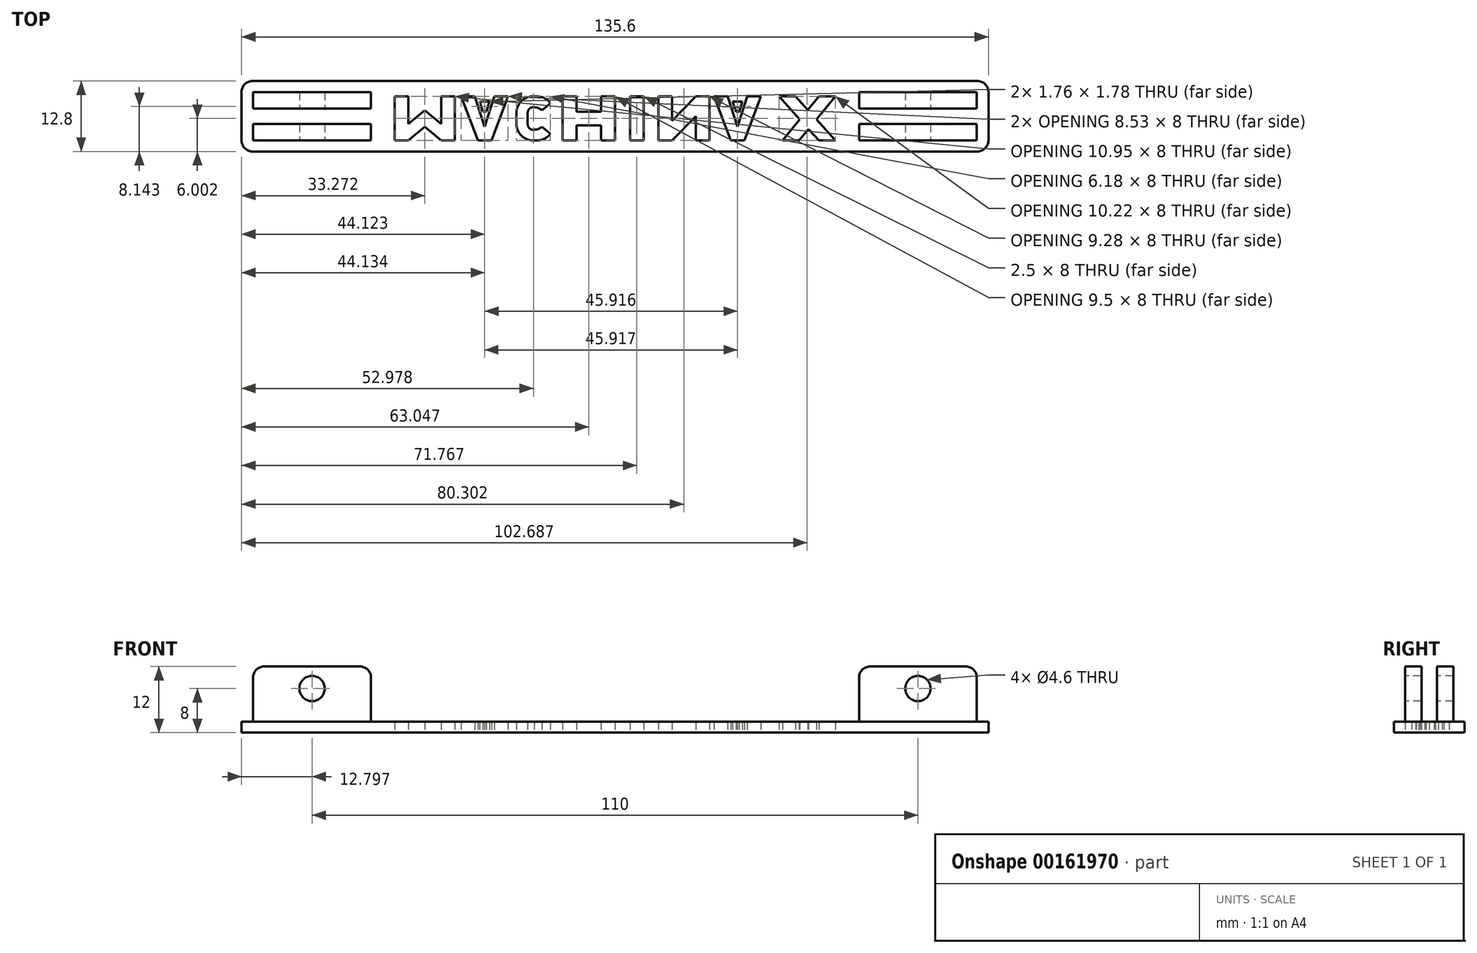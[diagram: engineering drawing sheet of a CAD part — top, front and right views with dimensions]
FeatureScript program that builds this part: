
annotation { "Feature Type Name" : "Feature", "Feature Type Description" : "" }
export const myFeature = defineFeature(function(context is Context, id is Id, definition is map)
    precondition{}
    {
        {
            var Q0;
            Q0=qCreatedBy(makeId("Top.planeOp"),FACE);
            var sketch = newSketch(context, id + "F0", { "sketchPlane" : qUnion([Q0])});
            skLineSegment(sketch, "E0.bottom", {"start": v(-66.14, 19.98) * mm, "end": v(65.46, 19.98) * mm});
            skLineSegment(sketch, "E0.top", {"start": v(-66.14, 7.18) * mm, "end": v(65.46, 7.18) * mm});
            skLineSegment(sketch, "E0.left", {"start": v(-68.14, 17.98) * mm, "end": v(-68.14, 9.18) * mm});
            skLineSegment(sketch, "E0.right", {"start": v(67.46, 17.98) * mm, "end": v(67.46, 9.18) * mm});
            skPoint(sketch, "E1.visualSharp", {"position": v(-68.14, 19.98) * mm});
            skArc(sketch, "E1.filletArc", {"start": v(-66.14, 19.98) * mm, "mid": v(-67.56, 19.4) * mm, "end": v(-68.14, 17.98) * mm});
            skPoint(sketch, "E2.visualSharp", {"position": v(-68.14, 7.18) * mm});
            skArc(sketch, "E2.filletArc", {"start": v(-68.14, 9.18) * mm, "mid": v(-67.56, 7.77) * mm, "end": v(-66.14, 7.18) * mm});
            skPoint(sketch, "E3.visualSharp", {"position": v(67.46, 19.98) * mm});
            skArc(sketch, "E3.filletArc", {"start": v(67.46, 17.98) * mm, "mid": v(66.87, 19.4) * mm, "end": v(65.46, 19.98) * mm});
            skPoint(sketch, "E4.visualSharp", {"position": v(67.46, 7.18) * mm});
            skArc(sketch, "E4.filletArc", {"start": v(65.46, 7.18) * mm, "mid": v(66.87, 7.77) * mm, "end": v(67.46, 9.18) * mm});
            skSolve(sketch);
        }
        {
            var Q0;
            Q0 = qSketchRegion(id + "F0", true);
            extrude(context, id + "F1", {"entities" : qUnion([Q0]), "depth" : 2 * mm});
        }
        {
            var Q0;
            Q0=makeQuery(id+"F1.opExtrude","CAP_FACE",FACE,{"disambiguationData":[OSD([sQuery(id+"F0.wireOp",EDGE,"E0.bottom"),sQuery(id+"F0.wireOp",EDGE,"E0.top"),sQuery(id+"F0.wireOp",EDGE,"E0.left"),sQuery(id+"F0.wireOp",EDGE,"E0.right"),sQuery(id+"F0.wireOp",EDGE,"E1.filletArc"),sQuery(id+"F0.wireOp",EDGE,"E2.filletArc"),sQuery(id+"F0.wireOp",EDGE,"E3.filletArc"),sQuery(id+"F0.wireOp",EDGE,"E4.filletArc")])],"isStart":false});
            var sketch = newSketch(context, id + "F2", { "sketchPlane" : qUnion([Q0])});
            skLineSegment(sketch, "E5.0", {"start": v(-68.14, 17.98) * mm, "end": v(-68.14, 9.18) * mm, "construction": true});
            skLineSegment(sketch, "E6.0", {"start": v(-66.14, 7.18) * mm, "end": v(65.46, 7.18) * mm, "construction": true});
            skLineSegment(sketch, "E7", {"start": v(-68.14, 13.58) * mm, "end": v(-66.04, 13.58) * mm, "construction": true});
            skPoint(sketch, "E7.endSnap0", {"position": v(-68.14, 13.58) * mm});
            skLineSegment(sketch, "E8", {"start": v(-66.04, 13.58) * mm, "end": v(-44.64, 13.58) * mm, "construction": true});
            skLineSegment(sketch, "E9", {"start": v(-44.64, 13.58) * mm, "end": v(43.96, 13.58) * mm, "construction": true});
            skLineSegment(sketch, "E10", {"start": v(43.96, 13.58) * mm, "end": v(65.36, 13.58) * mm, "construction": true});
            skLineSegment(sketch, "E11", {"start": v(65.36, 13.58) * mm, "end": v(67.46, 13.58) * mm, "construction": true});
            skLineSegment(sketch, "E12", {"start": v(-0.34, 7.18) * mm, "end": v(-0.34, 9.18) * mm, "construction": true});
            skLineSegment(sketch, "E13", {"start": v(-0.34, 9.18) * mm, "end": v(-0.34, 12.18) * mm, "construction": true});
            skLineSegment(sketch, "E14", {"start": v(-0.34, 12.18) * mm, "end": v(-0.34, 14.98) * mm, "construction": true});
            skPoint(sketch, "E14.endSnap0", {"position": v(-0.34, 10.68) * mm});
            skLineSegment(sketch, "E15", {"start": v(-0.34, 14.98) * mm, "end": v(-0.34, 17.98) * mm, "construction": true});
            skLineSegment(sketch, "E16", {"start": v(-0.34, 17.98) * mm, "end": v(-0.34, 19.98) * mm, "construction": true});
            skLineSegment(sketch, "E17.bottom", {"start": v(-66.04, 9.18) * mm, "end": v(-44.64, 9.18) * mm});
            skLineSegment(sketch, "E17.top", {"start": v(-66.04, 12.18) * mm, "end": v(-44.64, 12.18) * mm});
            skLineSegment(sketch, "E17.left", {"start": v(-66.04, 9.18) * mm, "end": v(-66.04, 12.18) * mm});
            skLineSegment(sketch, "E17.right", {"start": v(-44.64, 9.18) * mm, "end": v(-44.64, 12.18) * mm});
            skLineSegment(sketch, "E18.bottom", {"start": v(-66.04, 17.98) * mm, "end": v(-44.64, 17.98) * mm});
            skLineSegment(sketch, "E18.top", {"start": v(-66.04, 14.98) * mm, "end": v(-44.64, 14.98) * mm});
            skLineSegment(sketch, "E18.left", {"start": v(-66.04, 17.98) * mm, "end": v(-66.04, 14.98) * mm});
            skLineSegment(sketch, "E18.right", {"start": v(-44.64, 17.98) * mm, "end": v(-44.64, 14.98) * mm});
            skLineSegment(sketch, "E19.bottom", {"start": v(65.36, 17.98) * mm, "end": v(43.96, 17.98) * mm});
            skLineSegment(sketch, "E19.top", {"start": v(65.36, 14.98) * mm, "end": v(43.96, 14.98) * mm});
            skLineSegment(sketch, "E19.left", {"start": v(65.36, 17.98) * mm, "end": v(65.36, 14.98) * mm});
            skLineSegment(sketch, "E19.right", {"start": v(43.96, 17.98) * mm, "end": v(43.96, 14.98) * mm});
            skLineSegment(sketch, "E20.bottom", {"start": v(65.36, 9.18) * mm, "end": v(43.96, 9.18) * mm});
            skLineSegment(sketch, "E20.top", {"start": v(65.36, 12.18) * mm, "end": v(43.96, 12.18) * mm});
            skLineSegment(sketch, "E20.left", {"start": v(65.36, 9.18) * mm, "end": v(65.36, 12.18) * mm});
            skLineSegment(sketch, "E20.right", {"start": v(43.96, 9.18) * mm, "end": v(43.96, 12.18) * mm});
            skSolve(sketch);
        }
        {
            var Q0;
            Q0 = qSketchRegion(id + "F2", true);
            extrude(context, id + "F3", {"entities" : qUnion([Q0]), "operationType" : NewBodyOperationType.ADD, "depth" : 10 * mm});
        }
        {
            var Q0;
            Q0=makeQuery(id+"F3.opExtrude","CAP_EDGE",EDGE,{"disambiguationData":[OSD([sQuery(id+"F2.wireOp",EDGE,"E18.left")])],"isStart":false});
            var Q1;
            Q1=makeQuery(id+"F3.opExtrude","CAP_EDGE",EDGE,{"disambiguationData":[OSD([sQuery(id+"F2.wireOp",EDGE,"E17.left")])],"isStart":false});
            var Q2;
            Q2=makeQuery(id+"F3.opExtrude","CAP_EDGE",EDGE,{"disambiguationData":[OSD([sQuery(id+"F2.wireOp",EDGE,"E18.right")])],"isStart":false});
            var Q3;
            Q3=makeQuery(id+"F3.opExtrude","CAP_EDGE",EDGE,{"disambiguationData":[OSD([sQuery(id+"F2.wireOp",EDGE,"E17.right")])],"isStart":false});
            var Q4;
            Q4=makeQuery(id+"F3.opExtrude","CAP_EDGE",EDGE,{"disambiguationData":[OSD([sQuery(id+"F2.wireOp",EDGE,"E19.right")])],"isStart":false});
            var Q5;
            Q5=makeQuery(id+"F3.opExtrude","CAP_EDGE",EDGE,{"disambiguationData":[OSD([sQuery(id+"F2.wireOp",EDGE,"E19.left")])],"isStart":false});
            var Q6;
            Q6=makeQuery(id+"F3.opExtrude","CAP_EDGE",EDGE,{"disambiguationData":[OSD([sQuery(id+"F2.wireOp",EDGE,"E20.left")])],"isStart":false});
            var Q7;
            Q7=makeQuery(id+"F3.opExtrude","CAP_EDGE",EDGE,{"disambiguationData":[OSD([sQuery(id+"F2.wireOp",EDGE,"E20.right")])],"isStart":false});
            fillet(context, id + "F4", {"entities" : qUnion([Q0, Q1, Q2, Q3, Q4, Q5, Q6, Q7]), "radius" : 2 * mm, "tangentPropagation" : true, "allowEdgeOverflow" : false});
        }
        {
            var Q0;
            Q0=makeQuery(id+"F3.opExtrude","SWEPT_FACE",FACE,{"disambiguationData":[OSD([sQuery(id+"F2.wireOp",EDGE,"E17.bottom")])]});
            var sketch = newSketch(context, id + "F5", { "sketchPlane" : qUnion([Q0])});
            skLineSegment(sketch, "E21.0", {"start": v(-66.04, 2) * mm, "end": v(-44.64, 2) * mm, "construction": true});
            skLineSegment(sketch, "E22.0", {"start": v(65.36, 2) * mm, "end": v(43.96, 2) * mm, "construction": true});
            skLineSegment(sketch, "E23", {"start": v(-55.34, 2) * mm, "end": v(-55.34, 8) * mm, "construction": true});
            skLineSegment(sketch, "E24", {"start": v(54.66, 2) * mm, "end": v(54.66, 8) * mm, "construction": true});
            skPoint(sketch, "E24.endSnap0", {"position": v(54.66, 2) * mm});
            skCircle(sketch, "E25", {"center": v(-55.34, 8) * mm, "radius": 2.3 * mm});
            skCircle(sketch, "E26", {"center": v(54.66, 8) * mm, "radius": 2.3 * mm});
            skSolve(sketch);
        }
        {
            var Q0;
            Q0 = qSketchRegion(id + "F5", true);
            extrude(context, id + "F6", {"entities" : qUnion([Q0]), "operationType" : NewBodyOperationType.REMOVE, "oppositeDirection" : true, "depth" : 25 * mm});
        }
        {
            var Q0;
            Q0=makeQuery(id+"F1.opExtrude","CAP_FACE",FACE,{"disambiguationData":[OSD([sQuery(id+"F0.wireOp",EDGE,"E0.bottom"),sQuery(id+"F0.wireOp",EDGE,"E0.top"),sQuery(id+"F0.wireOp",EDGE,"E0.left"),sQuery(id+"F0.wireOp",EDGE,"E0.right"),sQuery(id+"F0.wireOp",EDGE,"E1.filletArc"),sQuery(id+"F0.wireOp",EDGE,"E2.filletArc"),sQuery(id+"F0.wireOp",EDGE,"E3.filletArc"),sQuery(id+"F0.wireOp",EDGE,"E4.filletArc")])],"isStart":true});
            var sketch = newSketch(context, id + "F7", { "sketchPlane" : qUnion([Q0])});
            skLineSegment(sketch, "E27.bottom", {"start": v(-40.34, -9.18) * mm, "end": v(39.66, -9.18) * mm, "construction": true});
            skLineSegment(sketch, "E27.top", {"start": v(-40.34, -17.18) * mm, "end": v(39.66, -17.18) * mm, "construction": true});
            skLineSegment(sketch, "E27.left", {"start": v(-40.34, -9.18) * mm, "end": v(-40.34, -17.18) * mm, "construction": true});
            skLineSegment(sketch, "E27.right", {"start": v(39.66, -9.18) * mm, "end": v(39.66, -17.18) * mm, "construction": true});
            skPoint(sketch, "E28", {"position": v(-0.34, -9.18) * mm});
            skPoint(sketch, "E29", {"position": v(-0.34, -17.18) * mm});
            skPoint(sketch, "E30", {"position": v(-40.34, -13.18) * mm});
            skPoint(sketch, "E31", {"position": v(-68.14, -13.58) * mm});
            skPoint(sketch, "E32", {"position": v(67.46, -13.58) * mm});
            skPoint(sketch, "E33", {"position": v(-0.34, -7.18) * mm});
            skLineSegment(sketch, "E34.bottom", {"start": v(-40.34, -9.18) * mm, "end": v(-37.84, -9.18) * mm});
            skLineSegment(sketch, "E34.top", {"start": v(-40.34, -17.18) * mm, "end": v(-37.84, -17.18) * mm});
            skLineSegment(sketch, "E34.left", {"start": v(-40.34, -9.18) * mm, "end": v(-40.34, -17.18) * mm});
            skLineSegment(sketch, "E34.right", {"start": v(-37.84, -12.18) * mm, "end": v(-37.84, -17.18) * mm});
            skLineSegment(sketch, "E35.bottom", {"start": v(-29.4, -9.18) * mm, "end": v(-31.9, -9.18) * mm});
            skLineSegment(sketch, "E35.top", {"start": v(-29.4, -17.18) * mm, "end": v(-31.9, -17.18) * mm});
            skLineSegment(sketch, "E35.left", {"start": v(-29.4, -9.18) * mm, "end": v(-29.4, -17.18) * mm});
            skLineSegment(sketch, "E35.right", {"start": v(-31.9, -12.18) * mm, "end": v(-31.9, -17.18) * mm});
            skLineSegment(sketch, "E36", {"start": v(-31.9, -9.18) * mm, "end": v(-34.87, -11.67) * mm});
            skLineSegment(sketch, "E37", {"start": v(-34.87, -11.67) * mm, "end": v(-37.84, -9.18) * mm});
            skLineSegment(sketch, "E38", {"start": v(-37.84, -12.18) * mm, "end": v(-34.87, -14.67) * mm});
            skLineSegment(sketch, "E39", {"start": v(-34.87, -14.67) * mm, "end": v(-31.9, -12.18) * mm});
            skLineSegment(sketch, "E40", {"start": v(-28.28, -17.18) * mm, "end": v(-25.24, -9.18) * mm});
            skLineSegment(sketch, "E41", {"start": v(-25.24, -9.18) * mm, "end": v(-22.74, -9.18) * mm});
            skLineSegment(sketch, "E42", {"start": v(-22.74, -9.18) * mm, "end": v(-19.75, -17.18) * mm});
            skLineSegment(sketch, "E43", {"start": v(-19.75, -17.18) * mm, "end": v(-22.25, -17.18) * mm});
            skLineSegment(sketch, "E44", {"start": v(-22.25, -17.18) * mm, "end": v(-24, -11.68) * mm});
            skPoint(sketch, "E44.endSnap0", {"position": v(-24, -9.18) * mm});
            skLineSegment(sketch, "E45", {"start": v(-24, -11.68) * mm, "end": v(-25.78, -17.18) * mm});
            skLineSegment(sketch, "E46", {"start": v(-25.78, -17.18) * mm, "end": v(-28.28, -17.18) * mm});
            skLineSegment(sketch, "E47", {"start": v(-24.89, -16.21) * mm, "end": v(-23.12, -16.21) * mm});
            skPoint(sketch, "E47.startSnap0", {"position": v(-24.89, -14.43) * mm});
            skPoint(sketch, "E47.endSnap0", {"position": v(-23.12, -14.43) * mm});
            skLineSegment(sketch, "E48", {"start": v(-23.12, -16.21) * mm, "end": v(-23.69, -14.43) * mm});
            skLineSegment(sketch, "E49", {"start": v(-23.69, -14.43) * mm, "end": v(-24.3, -14.43) * mm});
            skLineSegment(sketch, "E50", {"start": v(-24.3, -14.43) * mm, "end": v(-24.89, -16.21) * mm});
            skLineSegment(sketch, "E51", {"start": v(-18.25, -12.18) * mm, "end": v(-18.25, -14.18) * mm});
            skLineSegment(sketch, "E52", {"start": v(-15.25, -17.18) * mm, "end": v(-14.5, -17.18) * mm});
            skLineSegment(sketch, "E53", {"start": v(-14.48, -9.18) * mm, "end": v(-15.25, -9.18) * mm});
            skPoint(sketch, "E54.visualSharp", {"position": v(-18.25, -9.18) * mm});
            skArc(sketch, "E54.filletArc", {"start": v(-15.25, -9.18) * mm, "mid": v(-17.37, -10.06) * mm, "end": v(-18.25, -12.18) * mm});
            skPoint(sketch, "E55.visualSharp", {"position": v(-18.25, -17.18) * mm});
            skArc(sketch, "E55.filletArc", {"start": v(-18.25, -14.18) * mm, "mid": v(-17.37, -16.3) * mm, "end": v(-15.25, -17.18) * mm});
            skPoint(sketch, "E56.visualSharp", {"position": v(-11.25, -17.18) * mm});
            skArc(sketch, "E56.filletArc", {"start": v(-14.5, -17.18) * mm, "mid": v(-13.14, -16.86) * mm, "end": v(-12.07, -15.95) * mm});
            skPoint(sketch, "E57.visualSharp", {"position": v(-12.25, -9.18) * mm});
            skArc(sketch, "E57.filletArc", {"start": v(-12.07, -10.4) * mm, "mid": v(-13.13, -9.5) * mm, "end": v(-14.48, -9.18) * mm});
            skLineSegment(sketch, "E58", {"start": v(-15.19, -12.11) * mm, "end": v(-15.25, -12.18) * mm});
            skPoint(sketch, "E59.endSnap0", {"position": v(-13.77, -15.2) * mm});
            skLineSegment(sketch, "E60", {"start": v(-16.19, -14.22) * mm, "end": v(-16.19, -12.11) * mm});
            skPoint(sketch, "E61.visualSharp", {"position": v(-16.19, -11.12) * mm});
            skArc(sketch, "E61.filletArc", {"start": v(-14.97, -11.14) * mm, "mid": v(-15.81, -11.33) * mm, "end": v(-16.19, -12.11) * mm});
            skPoint(sketch, "E62.visualSharp", {"position": v(-16.19, -15.2) * mm});
            skArc(sketch, "E62.filletArc", {"start": v(-16.19, -14.22) * mm, "mid": v(-15.81, -15) * mm, "end": v(-14.97, -15.2) * mm});
            skLineSegment(sketch, "E63", {"start": v(-15.09, -11.14) * mm, "end": v(-14.97, -11.14) * mm});
            skLineSegment(sketch, "E64", {"start": v(-12.97, -13.14) * mm, "end": v(-12.97, -13.2) * mm});
            skLineSegment(sketch, "E65", {"start": v(-14.97, -15.2) * mm, "end": v(-14.97, -15.2) * mm});
            skPoint(sketch, "E66.visualSharp", {"position": v(-12.97, -11.14) * mm});
            skArc(sketch, "E66.filletArc", {"start": v(-13.61, -11.67) * mm, "mid": v(-14.24, -11.27) * mm, "end": v(-14.97, -11.14) * mm});
            skPoint(sketch, "E67.visualSharp", {"position": v(-12.97, -15.2) * mm});
            skArc(sketch, "E67.filletArc", {"start": v(-14.97, -15.2) * mm, "mid": v(-14.24, -15.06) * mm, "end": v(-13.61, -14.67) * mm});
            skLineSegment(sketch, "E68", {"start": v(-13.61, -11.67) * mm, "end": v(-12.07, -10.4) * mm});
            skLineSegment(sketch, "E69", {"start": v(-13.61, -14.67) * mm, "end": v(-12.07, -15.95) * mm});
            skPoint(sketch, "E70.orphan", {"position": v(-12.3, -16.22) * mm});
            skLineSegment(sketch, "E71.trimOffspring", {"start": v(-15.19, -14.22) * mm, "end": v(-15.25, -14.18) * mm});
            skPoint(sketch, "E72.orphan", {"position": v(-12.97, -9.59) * mm});
            skLineSegment(sketch, "E73.bottom", {"start": v(-9.84, -9.18) * mm, "end": v(-7.34, -9.18) * mm});
            skLineSegment(sketch, "E73.top", {"start": v(-9.84, -17.18) * mm, "end": v(-7.34, -17.18) * mm});
            skLineSegment(sketch, "E73.left", {"start": v(-9.84, -9.18) * mm, "end": v(-9.84, -17.18) * mm});
            skLineSegment(sketch, "E73.right", {"start": v(-7.34, -9.18) * mm, "end": v(-7.34, -11.93) * mm});
            skLineSegment(sketch, "E74.bottom", {"start": v(-2.84, -9.18) * mm, "end": v(-0.34, -9.18) * mm});
            skLineSegment(sketch, "E74.top", {"start": v(-2.84, -17.18) * mm, "end": v(-0.34, -17.18) * mm});
            skLineSegment(sketch, "E74.left", {"start": v(-2.84, -9.18) * mm, "end": v(-2.84, -11.93) * mm});
            skLineSegment(sketch, "E74.right", {"start": v(-0.34, -9.18) * mm, "end": v(-0.34, -17.18) * mm});
            skLineSegment(sketch, "E75.bottom", {"start": v(-7.34, -11.93) * mm, "end": v(-2.84, -11.93) * mm});
            skLineSegment(sketch, "E75.top", {"start": v(-7.34, -14.43) * mm, "end": v(-2.84, -14.43) * mm});
            skPoint(sketch, "E76", {"position": v(-7.34, -13.18) * mm});
            skPoint(sketch, "E77", {"position": v(-2.84, -13.18) * mm});
            skLineSegment(sketch, "E78.bottom", {"start": v(2.38, -9.18) * mm, "end": v(4.88, -9.18) * mm});
            skLineSegment(sketch, "E78.top", {"start": v(2.38, -17.18) * mm, "end": v(4.88, -17.18) * mm});
            skLineSegment(sketch, "E78.left", {"start": v(2.38, -9.18) * mm, "end": v(2.38, -17.18) * mm});
            skLineSegment(sketch, "E78.right", {"start": v(4.88, -9.18) * mm, "end": v(4.88, -17.18) * mm});
            skLineSegment(sketch, "E79.bottom", {"start": v(7.52, -9.18) * mm, "end": v(10.02, -9.18) * mm});
            skLineSegment(sketch, "E79.top", {"start": v(7.52, -17.18) * mm, "end": v(10.02, -17.18) * mm});
            skLineSegment(sketch, "E79.left", {"start": v(7.52, -9.18) * mm, "end": v(7.52, -17.18) * mm});
            skLineSegment(sketch, "E79.right", {"start": v(10.02, -12.77) * mm, "end": v(10.02, -17.18) * mm});
            skLineSegment(sketch, "E80.bottom", {"start": v(14.3, -9.18) * mm, "end": v(16.8, -9.18) * mm});
            skLineSegment(sketch, "E80.top", {"start": v(14.3, -17.18) * mm, "end": v(16.8, -17.18) * mm});
            skLineSegment(sketch, "E80.left", {"start": v(14.3, -9.18) * mm, "end": v(14.3, -13.6) * mm});
            skLineSegment(sketch, "E80.right", {"start": v(16.8, -9.18) * mm, "end": v(16.8, -17.18) * mm});
            skLineSegment(sketch, "E81", {"start": v(10.02, -9.18) * mm, "end": v(14.3, -13.6) * mm});
            skLineSegment(sketch, "E82", {"start": v(14.3, -17.18) * mm, "end": v(10.02, -12.77) * mm});
            skLineSegment(sketch, "E83", {"start": v(17.64, -17.18) * mm, "end": v(20.67, -9.18) * mm});
            skLineSegment(sketch, "E84", {"start": v(23.17, -9.18) * mm, "end": v(26.16, -17.18) * mm});
            skLineSegment(sketch, "E85", {"start": v(23.66, -17.18) * mm, "end": v(21.92, -11.68) * mm});
            skLineSegment(sketch, "E86", {"start": v(21.92, -11.68) * mm, "end": v(20.14, -17.18) * mm});
            skLineSegment(sketch, "E87", {"start": v(22.8, -16.21) * mm, "end": v(22.23, -14.43) * mm});
            skLineSegment(sketch, "E88", {"start": v(21.6, -14.43) * mm, "end": v(21.03, -16.21) * mm});
            skLineSegment(sketch, "E89", {"start": v(20.67, -9.18) * mm, "end": v(23.17, -9.18) * mm});
            skLineSegment(sketch, "E90", {"start": v(17.64, -17.18) * mm, "end": v(20.14, -17.18) * mm});
            skLineSegment(sketch, "E91", {"start": v(23.66, -17.18) * mm, "end": v(26.16, -17.18) * mm});
            skLineSegment(sketch, "E92", {"start": v(21.03, -16.21) * mm, "end": v(22.8, -16.21) * mm});
            skLineSegment(sketch, "E93", {"start": v(21.6, -14.43) * mm, "end": v(22.23, -14.43) * mm});
            skLineSegment(sketch, "E94", {"start": v(29.44, -17.18) * mm, "end": v(33.22, -13) * mm});
            skLineSegment(sketch, "E95", {"start": v(36.66, -9.18) * mm, "end": v(39.66, -9.18) * mm});
            skLineSegment(sketch, "E96", {"start": v(39.66, -9.18) * mm, "end": v(36.22, -13) * mm});
            skLineSegment(sketch, "E97", {"start": v(32.44, -17.18) * mm, "end": v(29.44, -17.18) * mm});
            skLineSegment(sketch, "E98", {"start": v(39.66, -17.18) * mm, "end": v(36.22, -13) * mm});
            skLineSegment(sketch, "E99", {"start": v(33.1, -9.18) * mm, "end": v(30.1, -9.18) * mm});
            skLineSegment(sketch, "E100", {"start": v(30.1, -9.18) * mm, "end": v(33.22, -13) * mm});
            skLineSegment(sketch, "E101", {"start": v(36.66, -17.18) * mm, "end": v(39.66, -17.18) * mm});
            skLineSegment(sketch, "E102.trimOffspring", {"start": v(34.8, -11.25) * mm, "end": v(33.1, -9.18) * mm});
            skLineSegment(sketch, "E103.trimOffspring", {"start": v(34.65, -14.73) * mm, "end": v(36.66, -17.18) * mm});
            skLineSegment(sketch, "E104.trimOffspring", {"start": v(34.8, -11.25) * mm, "end": v(36.66, -9.18) * mm});
            skLineSegment(sketch, "E105.trimOffspring", {"start": v(34.65, -14.73) * mm, "end": v(32.44, -17.18) * mm});
            skLineSegment(sketch, "E106.trimOffspring", {"start": v(-7.34, -14.43) * mm, "end": v(-7.34, -17.18) * mm});
            skLineSegment(sketch, "E107.trimOffspring", {"start": v(-2.84, -14.43) * mm, "end": v(-2.84, -17.18) * mm});
            skSolve(sketch);
        }
        {
            var Q0;
            Q0 = qSketchRegion(id + "F7", true);
            extrude(context, id + "F8", {"entities" : qUnion([Q0]), "operationType" : NewBodyOperationType.REMOVE, "oppositeDirection" : true, "depth" : 25 * mm});
        }
    });
